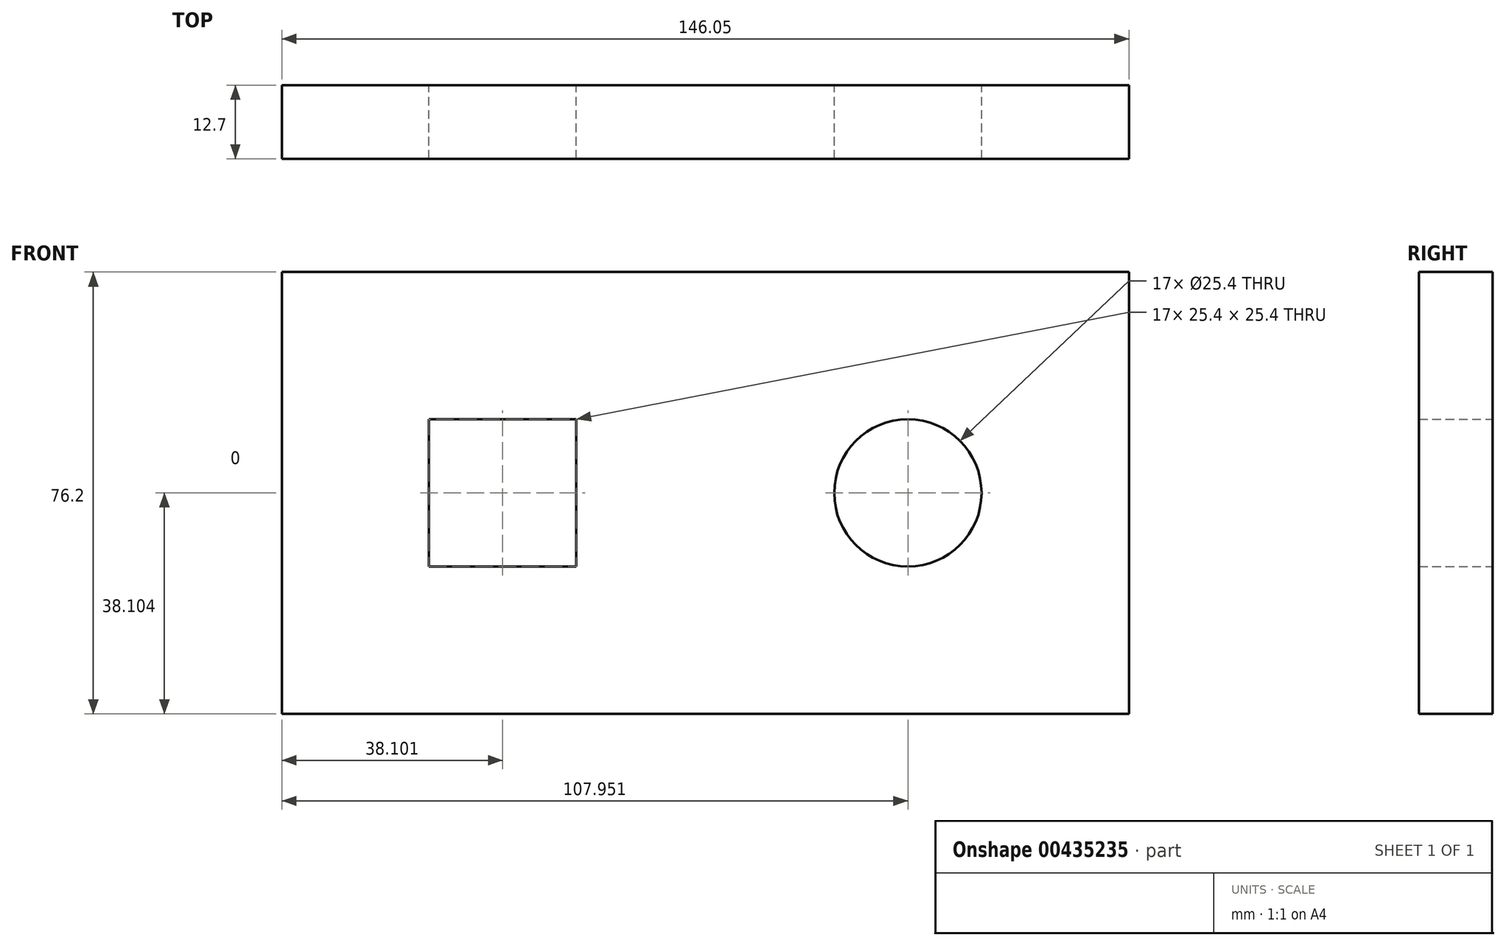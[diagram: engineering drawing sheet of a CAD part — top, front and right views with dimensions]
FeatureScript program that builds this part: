
annotation { "Feature Type Name" : "Feature", "Feature Type Description" : "" }
export const myFeature = defineFeature(function(context is Context, id is Id, definition is map)
    precondition{}
    {
        {
            var Q0;
            Q0=qCreatedBy(makeId("Front.planeOp"),FACE);
            var sketch = newSketch(context, id + "F0", { "sketchPlane" : qUnion([Q0])});
            skLineSegment(sketch, "E0", {"start": v(-53.85, 68.94) * mm, "end": v(-53.85, -7.26) * mm});
            skLineSegment(sketch, "E1", {"start": v(-53.85, 68.94) * mm, "end": v(92.2, 68.94) * mm});
            skLineSegment(sketch, "E2", {"start": v(92.2, 68.94) * mm, "end": v(92.2, -7.26) * mm});
            skLineSegment(sketch, "E3", {"start": v(92.2, -7.26) * mm, "end": v(-53.85, -7.26) * mm});
            skCircle(sketch, "E4", {"center": v(54.1, 30.84) * mm, "radius": 12.7 * mm});
            skLineSegment(sketch, "E5.bottom", {"start": v(-28.45, 43.54) * mm, "end": v(-3.05, 43.54) * mm});
            skLineSegment(sketch, "E5.top", {"start": v(-28.45, 18.14) * mm, "end": v(-3.05, 18.14) * mm});
            skLineSegment(sketch, "E5.left", {"start": v(-28.45, 43.54) * mm, "end": v(-28.45, 18.14) * mm});
            skLineSegment(sketch, "E5.right", {"start": v(-3.05, 43.54) * mm, "end": v(-3.05, 18.14) * mm});
            skSolve(sketch);
        }
        {
            var Q0;
            Q0 = qSketchRegion(id + "F0", true);
            extrude(context, id + "F1", {"entities" : qUnion([Q0]), "depth" : 12.7 * mm});
        }
    });
